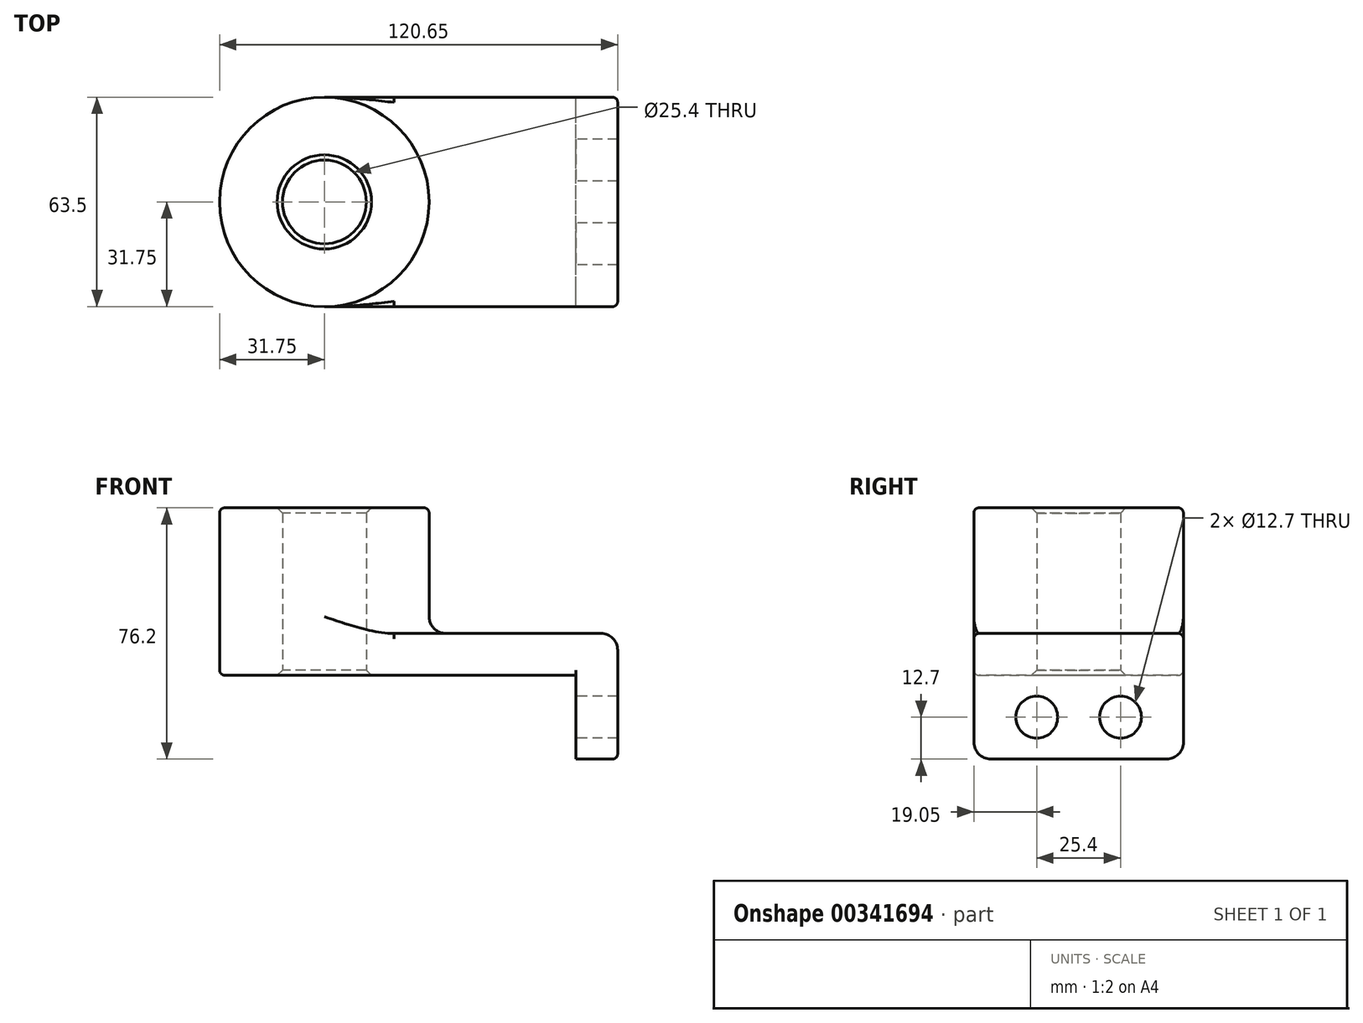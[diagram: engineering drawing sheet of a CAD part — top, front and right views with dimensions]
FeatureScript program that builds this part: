
annotation { "Feature Type Name" : "Feature", "Feature Type Description" : "" }
export const myFeature = defineFeature(function(context is Context, id is Id, definition is map)
    precondition{}
    {
        {
            var Q0;
            Q0=qCreatedBy(makeId("Top.planeOp"),FACE);
            var sketch = newSketch(context, id + "F0", { "sketchPlane" : qUnion([Q0])});
            skLineSegment(sketch, "E0.bottom", {"start": v(38.1, -31.75) * mm, "end": v(-38.1, -31.75) * mm});
            skLineSegment(sketch, "E0.top", {"start": v(38.1, 31.75) * mm, "end": v(-38.1, 31.75) * mm});
            skLineSegment(sketch, "E0.left", {"start": v(38.1, -31.75) * mm, "end": v(38.1, 31.75) * mm});
            skLineSegment(sketch, "E0.right", {"start": v(-38.1, -31.75) * mm, "end": v(-38.1, 31.75) * mm});
            skPoint(sketch, "E0.middle", {"position": v(0, 0) * mm});
            skCircle(sketch, "E1", {"center": v(-38.1, 0) * mm, "radius": 31.75 * mm});
            skCircle(sketch, "E2", {"center": v(-38.1, 0) * mm, "radius": 12.7 * mm});
            skSolve(sketch);
        }
        {
            var Q0;
            Q0 = qSketchRegion(id + "F0", true);
            extrude(context, id + "F1", {"entities" : qUnion([Q0]), "depth" : 12.7 * mm});
        }
        {
            var Q0;
            {var subQ1=sQuery(id+"F0.wireOp",EDGE,"E0.right");var subQ3=sQuery(id+"F0.wireOp",EDGE,"E2");var subQ4=makeQuery(id+"F0.imprint","INTERSECT",VERTEX,{"disambiguationData":[OD(0.0)],"derivedFrom":[subQ1,subQ3]});Q0=makeQuery(id+"F0.imprint","IMPRINT",FACE,{"disambiguationData":[TD([[makeQuery(id+"F0.imprint","IMPRINT",EDGE,{"disambiguationData":[TD([[subQ4,1.0]])],"derivedFrom":subQ3}),-1.0]])]});}
            var Q1;
            {var subQ1=sQuery(id+"F0.wireOp",EDGE,"E0.right");var subQ3=sQuery(id+"F0.wireOp",EDGE,"E2");var subQ4=makeQuery(id+"F0.imprint","INTERSECT",VERTEX,{"disambiguationData":[OD(0.0)],"derivedFrom":[subQ1,subQ3]});Q1=makeQuery(id+"F0.imprint","IMPRINT",FACE,{"disambiguationData":[TD([[makeQuery(id+"F0.imprint","IMPRINT",EDGE,{"disambiguationData":[TD([[subQ4,-1.0]])],"derivedFrom":subQ3}),-1.0]])]});}
            extrude(context, id + "F2", {"entities" : qUnion([Q0, Q1]), "operationType" : NewBodyOperationType.ADD, "depth" : 50.8 * mm});
        }
        {
            var Q0;
            Q0=makeQuery(id+"F1.opExtrude","SWEPT_FACE",FACE,{"disambiguationData":[OSD([sQuery(id+"F0.wireOp",EDGE,"E0.left")])]});
            var sketch = newSketch(context, id + "F3", { "sketchPlane" : qUnion([Q0])});
            skLineSegment(sketch, "E3.bottom", {"start": v(-31.75, 12.7) * mm, "end": v(31.75, 12.7) * mm});
            skLineSegment(sketch, "E3.top", {"start": v(-31.75, -25.4) * mm, "end": v(31.75, -25.4) * mm});
            skLineSegment(sketch, "E3.left", {"start": v(-31.75, 12.7) * mm, "end": v(-31.75, -25.4) * mm});
            skLineSegment(sketch, "E3.right", {"start": v(31.75, 12.7) * mm, "end": v(31.75, -25.4) * mm});
            skCircle(sketch, "E4", {"center": v(-12.7, -12.7) * mm, "radius": 6.35 * mm});
            skLineSegment(sketch, "E5", {"start": v(0, 0) * mm, "end": v(0, -25.4) * mm});
            skCircle(sketch, "E6.MirrorC", {"center": v(12.7, -12.7) * mm, "radius": 6.35 * mm});
            skSolve(sketch);
        }
        {
            var Q0;
            Q0 = qSketchRegion(id + "F3", true);
            extrude(context, id + "F4", {"entities" : qUnion([Q0]), "operationType" : NewBodyOperationType.ADD, "depth" : 12.7 * mm});
        }
        {
            var Q0;
            {var subQ0=sQuery(id+"F0.wireOp",EDGE,"E1");Q0=makeQuery(id+"F2.boolean.opBoolean","INTERSECT",EDGE,{"derivedFrom":[makeQuery(id+"F1.opExtrude","CAP_FACE",FACE,{"disambiguationData":[OSD([sQuery(id+"F0.wireOp",EDGE,"E0.bottom"),sQuery(id+"F0.wireOp",EDGE,"E0.top"),sQuery(id+"F0.wireOp",EDGE,"E0.left"),subQ0,sQuery(id+"F0.wireOp",EDGE,"E2")])],"isStart":false}),makeQuery(id+"F2.opExtrude","SWEPT_FACE",FACE,{"disambiguationData":[OSD([subQ0])]})]});}
            var Q1;
            Q1=makeQuery(id+"F4.opExtrude","CAP_EDGE",EDGE,{"disambiguationData":[OSD([sQuery(id+"F3.wireOp",EDGE,"E3.bottom")])],"isStart":false});
            var Q2;
            Q2=makeQuery(id+"F4.opExtrude","SWEPT_EDGE",EDGE,{"disambiguationData":[OSD([sQuery(id+"F3.wireOp",EDGE,"E3.top"),sQuery(id+"F3.wireOp",EDGE,"E3.left")])]});
            var Q3;
            Q3=makeQuery(id+"F4.opExtrude","SWEPT_EDGE",EDGE,{"disambiguationData":[OSD([sQuery(id+"F3.wireOp",EDGE,"E3.top"),sQuery(id+"F3.wireOp",EDGE,"E3.right")])]});
            fillet(context, id + "F5", {"entities" : qUnion([Q0, Q1, Q2, Q3]), "radius" : 5.08 * mm, "tangentPropagation" : true, "allowEdgeOverflow" : false});
        }
        {
            var Q0;
            Q0=makeQuery(id+"F4.boolean.opBoolean","MERGE",EDGE,{"derivedFrom":[makeQuery(id+"F1.opExtrude","CAP_EDGE",EDGE,{"disambiguationData":[OSD([sQuery(id+"F0.wireOp",EDGE,"E0.bottom")])],"isStart":false}),makeQuery(id+"F4.opExtrude","SWEPT_EDGE",EDGE,{"disambiguationData":[OSD([sQuery(id+"F3.wireOp",EDGE,"E3.bottom"),sQuery(id+"F3.wireOp",EDGE,"E3.left")])]})]});
            var Q1;
            Q1=makeQuery(id+"F1.opExtrude","CAP_EDGE",EDGE,{"disambiguationData":[OSD([sQuery(id+"F0.wireOp",EDGE,"E0.bottom")])],"isStart":true});
            var Q2;
            Q2=makeQuery(id+"F1.opExtrude","CAP_EDGE",EDGE,{"disambiguationData":[OSD([sQuery(id+"F0.wireOp",EDGE,"E0.left")])],"isStart":true});
            fillet(context, id + "F6", {"entities" : qUnion([Q0, Q1, Q2]), "radius" : 1.59 * mm, "tangentPropagation" : true, "allowEdgeOverflow" : false});
        }
        {
            var Q0;
            {var subQ0=sQuery(id+"F0.wireOp",EDGE,"E2");Q0=makeQuery(id+"F2.boolean.opBoolean","MERGE",FACE,{"derivedFrom":[makeQuery(id+"F1.opExtrude","SWEPT_FACE",FACE,{"disambiguationData":[OSD([subQ0])]}),makeQuery(id+"F2.opExtrude","SWEPT_FACE",FACE,{"disambiguationData":[OSD([subQ0])]})]});}
            chamfer(context, id + "F7", {"entities" : qUnion([Q0]), "width" : 1.59 * mm, "tangentPropagation" : true});
        }
        {
            var Q0;
            Q0=makeQuery(id+"F2.opExtrude","CAP_EDGE",EDGE,{"disambiguationData":[OSD([sQuery(id+"F0.wireOp",EDGE,"E1")])],"isStart":false});
            fillet(context, id + "F8", {"entities" : qUnion([Q0]), "radius" : 1.59 * mm, "tangentPropagation" : true, "allowEdgeOverflow" : false});
        }
    });
